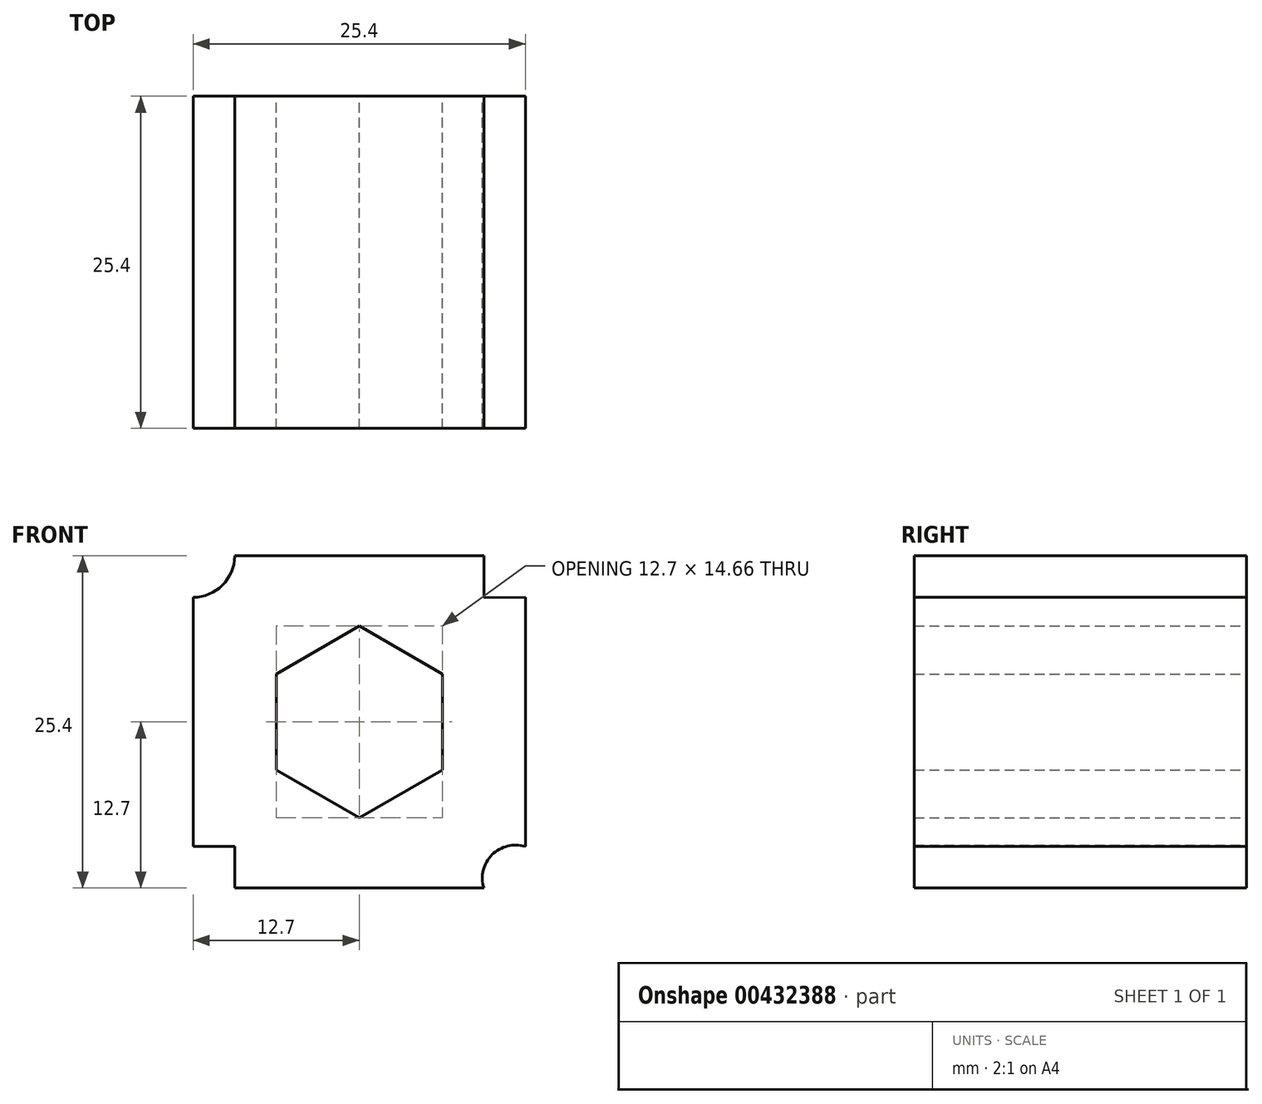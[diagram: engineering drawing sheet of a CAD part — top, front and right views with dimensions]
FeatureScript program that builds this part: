
annotation { "Feature Type Name" : "Feature", "Feature Type Description" : "" }
export const myFeature = defineFeature(function(context is Context, id is Id, definition is map)
    precondition{}
    {
        {
            var Q0;
            Q0=qCreatedBy(makeId("Front.planeOp"),FACE);
            var sketch = newSketch(context, id + "F0", { "sketchPlane" : qUnion([Q0])});
            skLineSegment(sketch, "E0.bottom", {"start": v(12.7, -12.7) * mm, "end": v(-12.7, -12.7) * mm});
            skLineSegment(sketch, "E0.top", {"start": v(12.7, 12.7) * mm, "end": v(-12.7, 12.7) * mm});
            skLineSegment(sketch, "E0.left", {"start": v(12.7, -12.7) * mm, "end": v(12.7, 12.7) * mm});
            skLineSegment(sketch, "E0.right", {"start": v(-12.7, -12.7) * mm, "end": v(-12.7, 12.7) * mm});
            skPoint(sketch, "E0.middle", {"position": v(0, 0) * mm});
            skCircle(sketch, "E1.cCircle", {"center": v(0, 0) * mm, "radius": 6.35 * mm, "construction": true});
            skLineSegment(sketch, "E1.0", {"start": v(6.35, -3.67) * mm, "end": v(0, -7.33) * mm});
            skLineSegment(sketch, "E1.1", {"start": v(0, -7.33) * mm, "end": v(-6.35, -3.67) * mm});
            skLineSegment(sketch, "E1.2", {"start": v(-6.35, -3.67) * mm, "end": v(-6.35, 3.67) * mm});
            skLineSegment(sketch, "E1.3", {"start": v(-6.35, 3.67) * mm, "end": v(0, 7.33) * mm});
            skLineSegment(sketch, "E1.4", {"start": v(0, 7.33) * mm, "end": v(6.35, 3.67) * mm});
            skLineSegment(sketch, "E1.5", {"start": v(6.35, 3.67) * mm, "end": v(6.35, -3.67) * mm});
            skPoint(sketch, "E1.0.midPoint", {"position": v(3.17, -5.5) * mm});
            skPoint(sketch, "E2", {"position": v(-9.52, 12.7) * mm});
            skPoint(sketch, "E3", {"position": v(-12.7, 9.53) * mm});
            skPoint(sketch, "E4", {"position": v(-12.7, -9.53) * mm});
            skPoint(sketch, "E5", {"position": v(12.7, -9.52) * mm});
            skPoint(sketch, "E6", {"position": v(12.7, 12.7) * mm});
            skPoint(sketch, "E7", {"position": v(12.7, 9.53) * mm});
            skPoint(sketch, "E8", {"position": v(-9.53, -12.7) * mm});
            skPoint(sketch, "E9", {"position": v(9.52, -12.7) * mm});
            skPoint(sketch, "E10", {"position": v(9.53, 12.7) * mm});
            skLineSegment(sketch, "E11", {"start": v(9.53, 12.7) * mm, "end": v(9.53, 9.52) * mm});
            skLineSegment(sketch, "E12", {"start": v(12.7, 9.52) * mm, "end": v(9.53, 9.52) * mm});
            skArc(sketch, "E13", {"start": v(-12.7, 9.53) * mm, "mid": v(-10.45, 10.45) * mm, "end": v(-9.52, 12.7) * mm});
            skArc(sketch, "E14", {"start": v(12.7, -9.52) * mm, "mid": v(10.16, -10.16) * mm, "end": v(9.52, -12.7) * mm});
            skLineSegment(sketch, "E15", {"start": v(-12.7, -9.53) * mm, "end": v(-9.53, -9.53) * mm});
            skLineSegment(sketch, "E16", {"start": v(-9.53, -9.53) * mm, "end": v(-9.53, -12.7) * mm});
            skSolve(sketch);
        }
        {
            var Q0;
            Q0=makeQuery(id+"F0.imprint","IMPRINT",FACE,{"disambiguationData":[TD([[makeQuery(id+"F0.imprint","IMPRINT",EDGE,{"derivedFrom":sQuery(id+"F0.wireOp",EDGE,"E1.0")}),1.0]])]});
            extrude(context, id + "F1", {"entities" : qUnion([Q0]), "depth" : 25.4 * mm});
        }
    });
